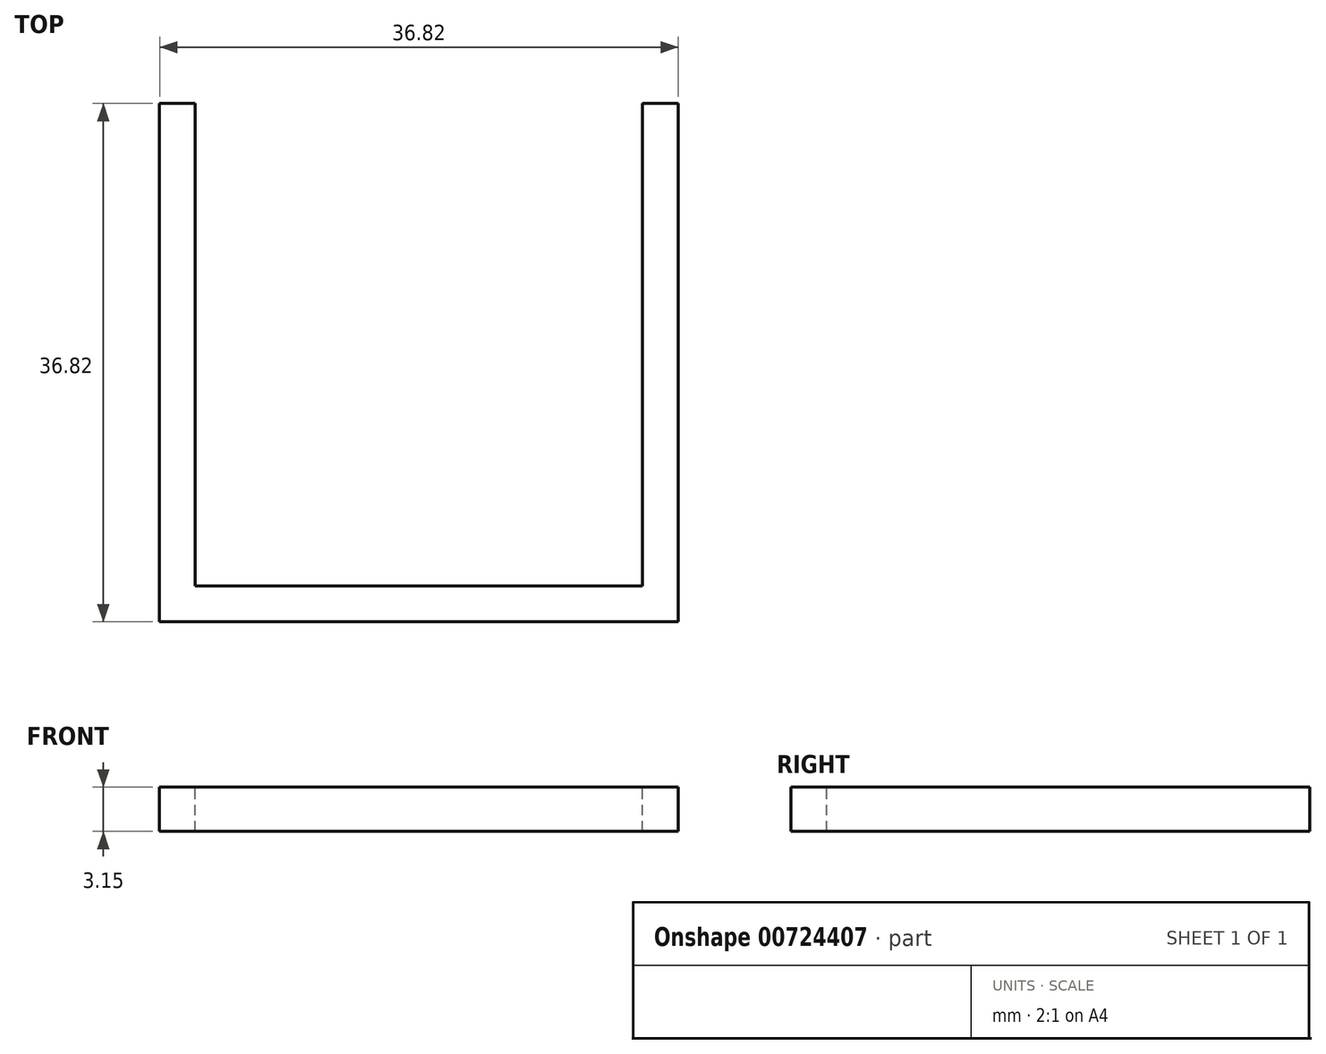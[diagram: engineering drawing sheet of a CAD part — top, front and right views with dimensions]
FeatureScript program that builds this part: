
annotation { "Feature Type Name" : "Feature", "Feature Type Description" : "" }
export const myFeature = defineFeature(function(context is Context, id is Id, definition is map)
    precondition{}
    {
        {
            var Q0;
            Q0=qCreatedBy(makeId("Top.planeOp"),FACE);
            var sketch = newSketch(context, id + "F0", { "sketchPlane" : qUnion([Q0])});
            skLineSegment(sketch, "E0.bottom", {"start": v(18.42, 18.41) * mm, "end": v(-18.41, 18.41) * mm});
            skLineSegment(sketch, "E0.top", {"start": v(18.42, -18.41) * mm, "end": v(-18.41, -18.41) * mm});
            skLineSegment(sketch, "E0.left", {"start": v(18.42, 18.41) * mm, "end": v(18.42, -18.41) * mm});
            skLineSegment(sketch, "E0.right", {"start": v(-18.41, 18.41) * mm, "end": v(-18.41, -18.41) * mm});
            skPoint(sketch, "E0.middle", {"position": v(0, 0) * mm});
            skSolve(sketch);
        }
        {
            var Q0;
            Q0=makeQuery(id+"F0.imprint","IMPRINT",FACE,{"disambiguationData":[TD([[makeQuery(id+"F0.imprint","IMPRINT",EDGE,{"derivedFrom":sQuery(id+"F0.wireOp",EDGE,"E0.bottom")}),1.0]])]});
            extrude(context, id + "F1", {"entities" : qUnion([Q0]), "depth" : 3.15 * mm, "offsetDistance" : 25.4 * mm});
        }
        {
            var Q0;
            Q0=makeQuery(id+"F1.opExtrude","CAP_FACE",FACE,{"disambiguationData":[OSD([sQuery(id+"F0.wireOp",EDGE,"E0.bottom"),sQuery(id+"F0.wireOp",EDGE,"E0.top"),sQuery(id+"F0.wireOp",EDGE,"E0.left"),sQuery(id+"F0.wireOp",EDGE,"E0.right")])],"isStart":false});
            var sketch = newSketch(context, id + "F2", { "sketchPlane" : qUnion([Q0])});
            skLineSegment(sketch, "E1.bottom", {"start": v(15.87, 15.88) * mm, "end": v(-15.88, 15.88) * mm});
            skLineSegment(sketch, "E1.top", {"start": v(15.88, -15.88) * mm, "end": v(-15.87, -15.88) * mm});
            skLineSegment(sketch, "E1.left", {"start": v(15.87, 15.88) * mm, "end": v(15.88, -15.88) * mm});
            skLineSegment(sketch, "E1.right", {"start": v(-15.88, 15.88) * mm, "end": v(-15.87, -15.88) * mm});
            skPoint(sketch, "E1.middle", {"position": v(0, 0) * mm});
            skSolve(sketch);
        }
        {
            var Q0;
            Q0=qSketchRegion(id+"F2",true);
            extrude(context, id + "F3", {"entities" : qUnion([Q0]), "operationType" : NewBodyOperationType.REMOVE, "oppositeDirection" : true, "depth" : 25.4 * mm, "offsetDistance" : 25.4 * mm});
        }
        {
            var Q0;
            Q0=makeQuery(id+"F1.opExtrude","CAP_FACE",FACE,{"disambiguationData":[OSD([sQuery(id+"F0.wireOp",EDGE,"E0.bottom"),sQuery(id+"F0.wireOp",EDGE,"E0.top"),sQuery(id+"F0.wireOp",EDGE,"E0.left"),sQuery(id+"F0.wireOp",EDGE,"E0.right")])],"isStart":false});
            var sketch = newSketch(context, id + "F4", { "sketchPlane" : qUnion([Q0])});
            skLineSegment(sketch, "E2.bottom", {"start": v(-15.88, 15.88) * mm, "end": v(15.87, 15.88) * mm});
            skLineSegment(sketch, "E2.top", {"start": v(-15.88, 18.41) * mm, "end": v(15.87, 18.41) * mm});
            skLineSegment(sketch, "E2.left", {"start": v(-15.88, 15.88) * mm, "end": v(-15.88, 18.41) * mm});
            skLineSegment(sketch, "E2.right", {"start": v(15.87, 15.88) * mm, "end": v(15.87, 18.41) * mm});
            skSolve(sketch);
        }
        {
            var Q0;
            Q0=makeQuery(id+"F4.imprint","IMPRINT",FACE,{"disambiguationData":[TD([[makeQuery(id+"F4.imprint","IMPRINT",EDGE,{"derivedFrom":sQuery(id+"F4.wireOp",EDGE,"E2.bottom")}),-1.0]])]});
            extrude(context, id + "F5", {"entities" : qUnion([Q0]), "operationType" : NewBodyOperationType.REMOVE, "oppositeDirection" : true, "depth" : 25.4 * mm, "offsetDistance" : 25.4 * mm});
        }
    });
